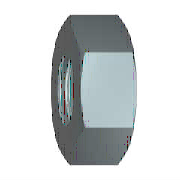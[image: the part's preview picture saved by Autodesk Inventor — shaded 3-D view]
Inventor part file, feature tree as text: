
AUTODESK INVENTOR PART (.ipt)
format: ipt  version: 2017 (Build 210142000, 142)  size: 174,080 bytes
history: native  units: mm (DEFAULTED — no unit token found)
features: sketch x3, chamfer x1, hole x1, other x1, plane x1
ambient origin geometry x7: Origin, YZ Plane, XZ Plane, X Axis, Y Axis, Z Axis, Center Point
bodies: Solid1 (feature_tree), Body (feature_tree)
feature tree (7):
  chamfer  "Chamfer1"  Angle=30.0deg  [1 undecoded]
  hole  "Thread"  [1 undecoded]
  other  "Work Axis1"
  plane  "Work Plane1"
  sketch  "Sketch1"  dims[d0=6.350853mm]
  sketch  "Sketch2"  dims[d1=2.9mm]
  sketch  "Sketch3"  dims[d2=0.0mm d3=30.0deg d4=30.0deg d5=5.5mm d6=5.5mm d7=90.0deg d25=2.459mm d26=6.0mm d27=4.0mm d28=2.0mm d29=14.3117mm d30=8.0mm d31=20.594885mm d8=0.270633mm d9=30.0deg d10=0.270633mm d11=30.0deg d13=0.0mm d14=0.0mm d39=0.0mm d40=0.270633mm d41=0.270633mm d42=0.0mm]
note: 2 required parameter values undecoded (feature->parameter linkage not recoverable at this tier; creation-order binding heuristic only, values carry confidence <= 0.55)
